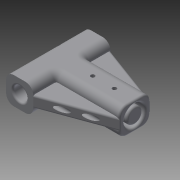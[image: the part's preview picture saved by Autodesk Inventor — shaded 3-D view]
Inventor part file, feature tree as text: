
AUTODESK INVENTOR PART (.ipt)
format: ipt  version: 2014 (Build 180170000, 170)  size: 667,136 bytes
history: native  units: mm
features: sketch x21, extrude x14, plane x7, fillet x6, emboss x1, other x1
ambient origin geometry x8: Origin, YZ Plane, XZ Plane, XY Plane, X Axis, Y Axis, Z Axis, Center Point
bodies: Solid1 (feature_tree)
feature tree (50):
  extrude  "Extrusion of Base"  Depth=50.8mm
  extrude  "Extrusion for 1 inch PVC"  Depth=25.4mm
  extrude  "Extrusion3"  Depth=34.0868mm
  plane  "Work Plane2"
  emboss  "Emboss1"
  plane  "Work Plane1"
  extrude  "Extrusion6"  Depth=114.55mm TaperAngle=0.0deg
  extrude  "Extrusion7"  Depth=152.4mm TaperAngle=0.0deg
  extrude  "Extrusion8"  Depth=2.0mm TaperAngle=0.0deg
  sketch  "Sketch15"  dims[d10=22.3012mm d11=152.4mm d12=0.0mm]
  sketch  "Sketch16"  dims[d25=13.0mm d26=2.0mm d27=0.0mm]
  plane  "Work Plane6"
  sketch  "Sketch18"  dims[d38=44.45mm d39=6.604mm]
  extrude  "Extrusion9"  Depth=6.604mm
  sketch  "Sketch20"  dims[d43=71.12mm d45=12.7mm d46=0.0mm]
  sketch  "Sketch21"  dims[d47=12.7mm d48=0.0mm d50=0.0mm]
  plane  "Work Plane8"
  extrude  "Extrusion13"  Depth=35.56mm
  extrude  "Extrusion16"  Depth=12.7mm TaperAngle=0.0deg
  extrude  "Extrusion17"  TaperAngle=0.0deg  [1 undecoded]
  sketch  "Sketch34"  dims[d85=114.55mm d86=0.0mm d87=19.05mm d88=0.0mm]
  sketch  "Sketch35"  dims[d89=8.0mm]
  plane  "Work Plane15"
  extrude  "Extrusion18"  TaperAngle=0.0deg  [1 undecoded]
  extrude  "Extrusion20"  Depth=5.0mm
  fillet  "Fillet25"  Radius=8.0mm
  fillet  "Fillet27"  Radius=143.0mm
  fillet  "Fillet28"  Radius=5.0mm
  fillet  "Fillet29"  Radius=38.1mm
  fillet  "Fillet30"  Radius=38.1mm
  fillet  "Fillet31"  Radius=8.0mm
  extrude  "Extrusion21"  Depth=50.8mm
  extrude  "Extrusion22"  Depth=19.05mm TaperAngle=0.0deg
  other  "Base for Part"
  sketch  "Sketch for 1 inch PVC"  dims[d107=3.175mm]
  sketch  "Sketch of Base Hole"  dims[d108=12.7mm d109=12.7mm d110=3.175mm d111=3.175mm d112=10.0mm d113=114.55mm d114=0.0mm d115=5.0mm d116=0.0mm]
  sketch  "Sketch5"  dims[d0=148.0mm d1=50.8mm]
  sketch  "Sketch9"  dims[d2=44.45mm d3=25.4mm]
  sketch  "Sketch10"  dims[d4=44.45mm d5=0.0mm d6=34.0868mm]
  sketch  "Sketch11"  dims[d7=25.3238mm d8=114.55mm d9=0.0mm]
  plane  "Work Plane5"
  sketch  "Sketch19"  dims[d40=44.45mm d41=0.0mm d42=35.56mm]
  plane  "Work Plane7"
  sketch  "Sketch29"  dims[d51=19.05mm d52=0.0mm d53=0.0mm]
  sketch  "Sketch32"  dims[d69=7.0mm d70=8.0mm d71=8.0mm d72=143.0mm d73=0.0mm d78=5.0mm d79=0.0mm d80=38.1mm d81=38.1mm d82=8.0mm]
  sketch  "Sketch33"  dims[d83=50.8mm d84=50.8mm]
  sketch  "Sketch36"  dims[d90=38.1mm]
  sketch  "Sketch37"  dims[d91=50.8mm]
  sketch  "Sketch38"  dims[d94=114.55mm d95=0.0mm]
  sketch  "Sketch39"  dims[d105=3.175mm]
note: 2 required parameter values undecoded (feature->parameter linkage not recoverable at this tier; creation-order binding heuristic only, values carry confidence <= 0.55)
